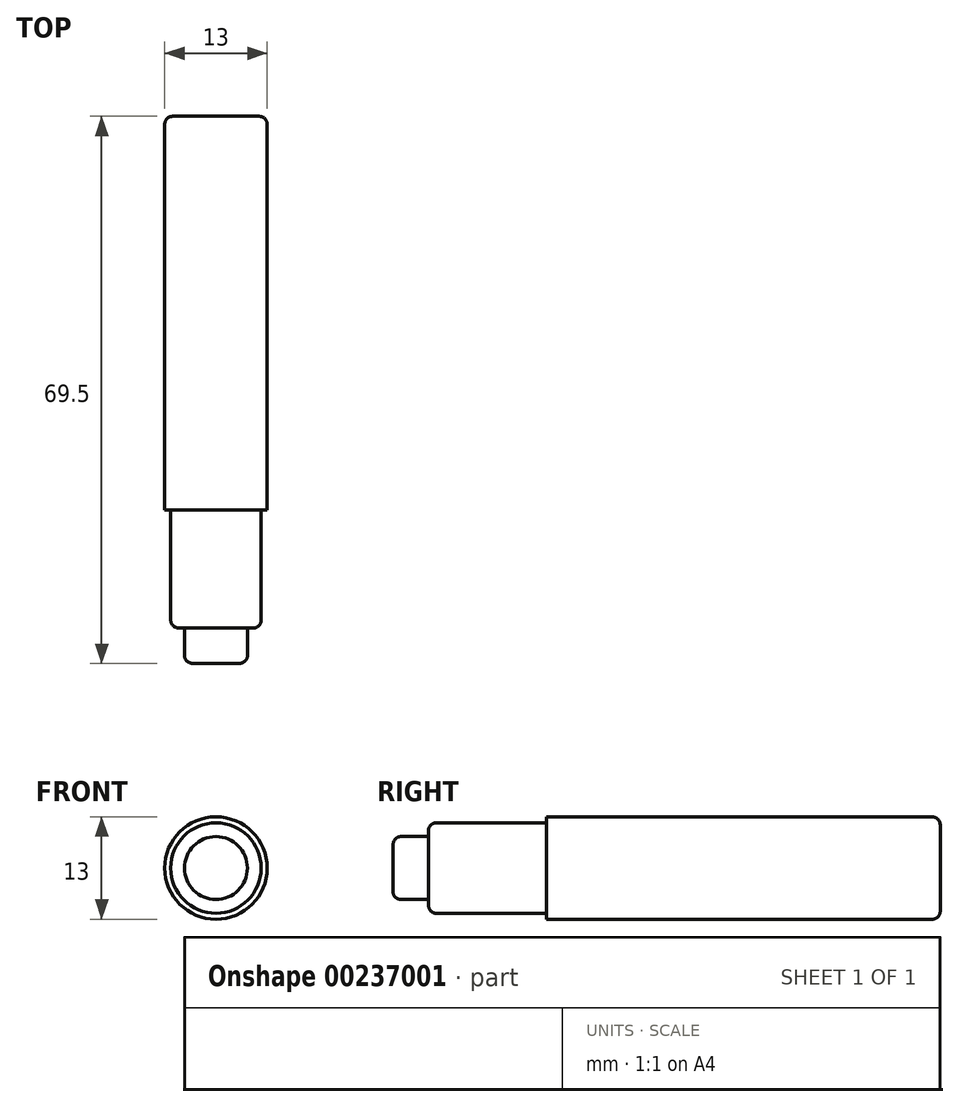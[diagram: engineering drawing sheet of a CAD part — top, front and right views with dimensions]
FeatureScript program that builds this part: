
annotation { "Feature Type Name" : "Feature", "Feature Type Description" : "" }
export const myFeature = defineFeature(function(context is Context, id is Id, definition is map)
    precondition{}
    {
        {
            var Q0;
            Q0=qCreatedBy(makeId("Front.planeOp"),FACE);
            var sketch = newSketch(context, id + "F0", { "sketchPlane" : qUnion([Q0])});
            skCircle(sketch, "E0", {"center": v(0, 0) * mm, "radius": 6.5 * mm});
            skSolve(sketch);
        }
        {
            var Q0;
            Q0 = qSketchRegion(id + "F0", true);
            var Q1;
            Q1=makeQuery(id+"F0.imprint","IMPRINT",FACE,{"disambiguationData":[TD([[makeQuery(id+"F0.imprint","IMPRINT",EDGE,{"derivedFrom":sQuery(id+"F0.wireOp",EDGE,"E0")}),1.0]])]});
            extrude(context, id + "F1", {"entities" : qUnion([Q0, Q1]), "depth" : 50 * mm});
        }
        {
            var Q0;
            Q0=makeQuery(id+"F1.opExtrude","CAP_FACE",FACE,{"disambiguationData":[OSD([sQuery(id+"F0.wireOp",EDGE,"E0")])],"isStart":false});
            var sketch = newSketch(context, id + "F2", { "sketchPlane" : qUnion([Q0])});
            skCircle(sketch, "E1", {"center": v(0, 0) * mm, "radius": 5.75 * mm});
            skSolve(sketch);
        }
        {
            var Q0;
            Q0=makeQuery(id+"F2.imprint","IMPRINT",FACE,{"disambiguationData":[TD([[makeQuery(id+"F2.imprint","IMPRINT",EDGE,{"derivedFrom":sQuery(id+"F2.wireOp",EDGE,"E1")}),1.0]])]});
            extrude(context, id + "F3", {"entities" : qUnion([Q0]), "operationType" : NewBodyOperationType.ADD, "depth" : 15 * mm});
        }
        {
            var Q0;
            Q0=makeQuery(id+"F3.opExtrude","CAP_FACE",FACE,{"disambiguationData":[OSD([sQuery(id+"F2.wireOp",EDGE,"E1")])],"isStart":false});
            var sketch = newSketch(context, id + "F4", { "sketchPlane" : qUnion([Q0])});
            skCircle(sketch, "E2", {"center": v(0, 0) * mm, "radius": 4 * mm});
            skSolve(sketch);
        }
        {
            var Q0;
            Q0=makeQuery(id+"F4.imprint","IMPRINT",FACE,{"disambiguationData":[TD([[makeQuery(id+"F4.imprint","IMPRINT",EDGE,{"derivedFrom":sQuery(id+"F4.wireOp",EDGE,"E2")}),1.0]])]});
            extrude(context, id + "F5", {"entities" : qUnion([Q0]), "operationType" : NewBodyOperationType.ADD, "depth" : 4.5 * mm});
        }
        {
            var Q0;
            Q0=makeQuery(id+"F5.opExtrude","CAP_EDGE",EDGE,{"disambiguationData":[OSD([sQuery(id+"F4.wireOp",EDGE,"E2")])],"isStart":false});
            var Q1;
            Q1=makeQuery(id+"F3.opExtrude","CAP_EDGE",EDGE,{"disambiguationData":[OSD([sQuery(id+"F2.wireOp",EDGE,"E1")])],"isStart":false});
            var Q2;
            Q2=makeQuery(id+"F1.opExtrude","CAP_EDGE",EDGE,{"disambiguationData":[OSD([sQuery(id+"F0.wireOp",EDGE,"E0")])],"isStart":true});
            fillet(context, id + "F6", {"entities" : qUnion([Q0, Q1, Q2]), "radius" : 1 * mm, "tangentPropagation" : true, "allowEdgeOverflow" : false});
        }
    });
